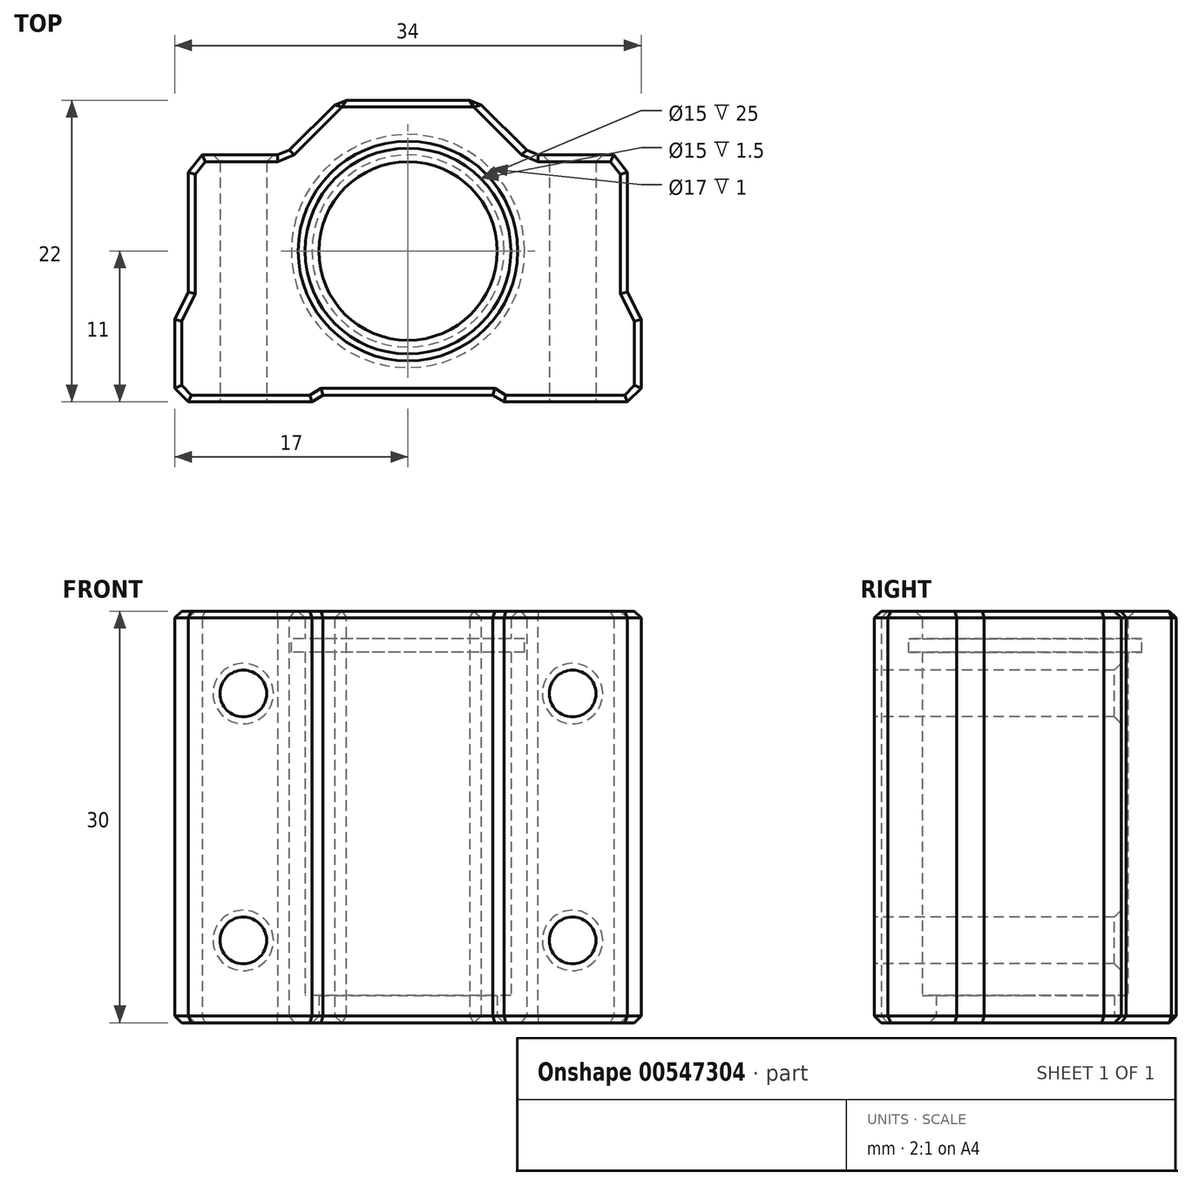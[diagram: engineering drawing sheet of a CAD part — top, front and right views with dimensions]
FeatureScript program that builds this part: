
annotation { "Feature Type Name" : "Feature", "Feature Type Description" : "" }
export const myFeature = defineFeature(function(context is Context, id is Id, definition is map)
    precondition{}
    {
        {
            var Q0;
            Q0=qCreatedBy(makeId("Top.planeOp"),FACE);
            var sketch = newSketch(context, id + "F0", { "sketchPlane" : qUnion([Q0])});
            skLineSegment(sketch, "E0", {"start": v(16, -11) * mm, "end": v(17, -10) * mm});
            skLineSegment(sketch, "E1", {"start": v(17, -10) * mm, "end": v(17, -5) * mm});
            skLineSegment(sketch, "E2", {"start": v(17, -5) * mm, "end": v(16, -3) * mm});
            skLineSegment(sketch, "E3", {"start": v(16, -3) * mm, "end": v(16, 5.75) * mm});
            skLineSegment(sketch, "E4", {"start": v(16, 5.75) * mm, "end": v(15, 7) * mm});
            skLineSegment(sketch, "E5", {"start": v(15, 7) * mm, "end": v(9, 7) * mm});
            skLineSegment(sketch, "E6", {"start": v(9, 7) * mm, "end": v(5, 11) * mm});
            skLineSegment(sketch, "E7", {"start": v(5, 11) * mm, "end": v(-5, 11) * mm});
            skLineSegment(sketch, "E8", {"start": v(-5, 11) * mm, "end": v(-9, 7) * mm});
            skLineSegment(sketch, "E9", {"start": v(-9, 7) * mm, "end": v(-15, 7) * mm});
            skLineSegment(sketch, "E10", {"start": v(-15, 7) * mm, "end": v(-16, 5.75) * mm});
            skLineSegment(sketch, "E11", {"start": v(-16, 5.75) * mm, "end": v(-16, -3) * mm});
            skLineSegment(sketch, "E12", {"start": v(-16, -3) * mm, "end": v(-17, -5) * mm});
            skLineSegment(sketch, "E13", {"start": v(-17, -5) * mm, "end": v(-17, -10) * mm});
            skLineSegment(sketch, "E14", {"start": v(-17, -10) * mm, "end": v(-16, -11) * mm});
            skCircle(sketch, "E15", {"center": v(0, 0) * mm, "radius": 7.5 * mm});
            skLineSegment(sketch, "E16", {"start": v(-16, -11) * mm, "end": v(-7, -11) * mm});
            skLineSegment(sketch, "E17", {"start": v(-7, -11) * mm, "end": v(-6.2, -10.5) * mm});
            skLineSegment(sketch, "E18", {"start": v(-6.2, -10.5) * mm, "end": v(6.2, -10.5) * mm});
            skLineSegment(sketch, "E19", {"start": v(6.2, -10.5) * mm, "end": v(7, -11) * mm});
            skLineSegment(sketch, "E20", {"start": v(7, -11) * mm, "end": v(16, -11) * mm});
            skSolve(sketch);
        }
        {
            var Q0;
            Q0 = qSketchRegion(id + "F0", true);
            extrude(context, id + "F1", {"entities" : qUnion([Q0]), "depth" : 15 * mm, "offsetDistance" : 25 * mm, "hasSecondDirection" : true, "secondDirectionOppositeDirection" : true, "secondDirectionDepth" : 15 * mm});
        }
        {
            var Q0;
            Q0=makeQuery(id+"F1.opExtrude","SWEPT_FACE",FACE,{"disambiguationData":[OSD([sQuery(id+"F0.wireOp",EDGE,"E16")])]});
            var sketch = newSketch(context, id + "F2", { "sketchPlane" : qUnion([Q0])});
            skCircle(sketch, "E21", {"center": v(-12, 9) * mm, "radius": 1.7 * mm});
            skCircle(sketch, "E22", {"center": v(-12, -9) * mm, "radius": 1.7 * mm});
            skCircle(sketch, "E23", {"center": v(12, 9) * mm, "radius": 1.7 * mm});
            skCircle(sketch, "E24", {"center": v(12, -9) * mm, "radius": 1.7 * mm});
            skSolve(sketch);
        }
        {
            var Q0;
            Q0=makeQuery(id+"F2.imprint","IMPRINT",FACE,{"disambiguationData":[TD([[makeQuery(id+"F2.imprint","IMPRINT",EDGE,{"derivedFrom":sQuery(id+"F2.wireOp",EDGE,"E21")}),1.0]])]});
            var Q1;
            Q1=makeQuery(id+"F2.imprint","IMPRINT",FACE,{"disambiguationData":[TD([[makeQuery(id+"F2.imprint","IMPRINT",EDGE,{"derivedFrom":sQuery(id+"F2.wireOp",EDGE,"E23")}),1.0]])]});
            var Q2;
            Q2=makeQuery(id+"F2.imprint","IMPRINT",FACE,{"disambiguationData":[TD([[makeQuery(id+"F2.imprint","IMPRINT",EDGE,{"derivedFrom":sQuery(id+"F2.wireOp",EDGE,"E24")}),1.0]])]});
            var Q3;
            Q3=makeQuery(id+"F2.imprint","IMPRINT",FACE,{"disambiguationData":[TD([[makeQuery(id+"F2.imprint","IMPRINT",EDGE,{"derivedFrom":sQuery(id+"F2.wireOp",EDGE,"E22")}),1.0]])]});
            var Q4;
            Q4=sQuery(id+"F2.wireOp",EDGE,"E22");
            var Q5;
            Q5=sQuery(id+"F2.wireOp",EDGE,"E21");
            var Q6;
            Q6=sQuery(id+"F2.wireOp",EDGE,"E23");
            var Q7;
            Q7=sQuery(id+"F2.wireOp",EDGE,"E24");
            extrude(context, id + "F3", {"entities" : qUnion([Q0, Q1, Q2, Q3]), "operationType" : NewBodyOperationType.REMOVE, "surfaceEntities" : qUnion([Q4, Q5, Q6, Q7]), "oppositeDirection" : true, "depth" : 25 * mm, "offsetDistance" : 25 * mm});
        }
        {
            var Q0;
            Q0=makeQuery(id+"F3.boolean.opBoolean","INTERSECT",EDGE,{"derivedFrom":[makeQuery(id+"F1.opExtrude","SWEPT_FACE",FACE,{"disambiguationData":[OSD([sQuery(id+"F0.wireOp",EDGE,"E9")])]}),makeQuery(id+"F3.opExtrude","SWEPT_FACE",FACE,{"disambiguationData":[OSD([sQuery(id+"F2.wireOp",EDGE,"E21")])]})]});
            var Q1;
            Q1=makeQuery(id+"F3.boolean.opBoolean","INTERSECT",EDGE,{"derivedFrom":[makeQuery(id+"F1.opExtrude","SWEPT_FACE",FACE,{"disambiguationData":[OSD([sQuery(id+"F0.wireOp",EDGE,"E9")])]}),makeQuery(id+"F3.opExtrude","SWEPT_FACE",FACE,{"disambiguationData":[OSD([sQuery(id+"F2.wireOp",EDGE,"E22")])]})]});
            var Q2;
            Q2=makeQuery(id+"F3.boolean.opBoolean","INTERSECT",EDGE,{"derivedFrom":[makeQuery(id+"F1.opExtrude","SWEPT_FACE",FACE,{"disambiguationData":[OSD([sQuery(id+"F0.wireOp",EDGE,"E5")])]}),makeQuery(id+"F3.opExtrude","SWEPT_FACE",FACE,{"disambiguationData":[OSD([sQuery(id+"F2.wireOp",EDGE,"E24")])]})]});
            var Q3;
            Q3=makeQuery(id+"F3.boolean.opBoolean","INTERSECT",EDGE,{"derivedFrom":[makeQuery(id+"F1.opExtrude","SWEPT_FACE",FACE,{"disambiguationData":[OSD([sQuery(id+"F0.wireOp",EDGE,"E5")])]}),makeQuery(id+"F3.opExtrude","SWEPT_FACE",FACE,{"disambiguationData":[OSD([sQuery(id+"F2.wireOp",EDGE,"E23")])]})]});
            var Q4;
            Q4=makeQuery(id+"F3.boolean.opBoolean","COPY",EDGE,{"derivedFrom":makeQuery(id+"F3.opExtrude","CAP_EDGE",EDGE,{"disambiguationData":[OSD([sQuery(id+"F2.wireOp",EDGE,"E21")])],"isStart":true})});
            var Q5;
            Q5=makeQuery(id+"F3.boolean.opBoolean","COPY",EDGE,{"derivedFrom":makeQuery(id+"F3.opExtrude","CAP_EDGE",EDGE,{"disambiguationData":[OSD([sQuery(id+"F2.wireOp",EDGE,"E22")])],"isStart":true})});
            var Q6;
            Q6=makeQuery(id+"F3.boolean.opBoolean","COPY",EDGE,{"derivedFrom":makeQuery(id+"F3.opExtrude","CAP_EDGE",EDGE,{"disambiguationData":[OSD([sQuery(id+"F2.wireOp",EDGE,"E24")])],"isStart":true})});
            var Q7;
            Q7=makeQuery(id+"F3.boolean.opBoolean","COPY",EDGE,{"derivedFrom":makeQuery(id+"F3.opExtrude","CAP_EDGE",EDGE,{"disambiguationData":[OSD([sQuery(id+"F2.wireOp",EDGE,"E23")])],"isStart":true})});
            chamfer(context, id + "F4", {"entities" : qUnion([Q0, Q1, Q2, Q3, Q4, Q5, Q6, Q7]), "width" : .5 * mm, "tangentPropagation" : true});
        }
        {
            var Q0;
            Q0=makeQuery(id+"F1.opExtrude","CAP_FACE",FACE,{"disambiguationData":[OSD([sQuery(id+"F0.wireOp",EDGE,"E0"),sQuery(id+"F0.wireOp",EDGE,"E1"),sQuery(id+"F0.wireOp",EDGE,"E2"),sQuery(id+"F0.wireOp",EDGE,"E3"),sQuery(id+"F0.wireOp",EDGE,"E4"),sQuery(id+"F0.wireOp",EDGE,"E5"),sQuery(id+"F0.wireOp",EDGE,"E6"),sQuery(id+"F0.wireOp",EDGE,"E7"),sQuery(id+"F0.wireOp",EDGE,"E8"),sQuery(id+"F0.wireOp",EDGE,"E9"),sQuery(id+"F0.wireOp",EDGE,"E10"),sQuery(id+"F0.wireOp",EDGE,"E11"),sQuery(id+"F0.wireOp",EDGE,"E12"),sQuery(id+"F0.wireOp",EDGE,"E13"),sQuery(id+"F0.wireOp",EDGE,"E14"),sQuery(id+"F0.wireOp",EDGE,"E15"),sQuery(id+"F0.wireOp",EDGE,"E16"),sQuery(id+"F0.wireOp",EDGE,"E17"),sQuery(id+"F0.wireOp",EDGE,"E18"),sQuery(id+"F0.wireOp",EDGE,"E19"),sQuery(id+"F0.wireOp",EDGE,"E20")])],"isStart":true});
            var sketch = newSketch(context, id + "F5", { "sketchPlane" : qUnion([Q0])});
            skCircle(sketch, "E25", {"center": v(0, 0) * mm, "radius": 6.5 * mm});
            skSolve(sketch);
        }
        {
            var Q0;
            Q0=makeQuery(id+"F5.imprint","IMPRINT",FACE,{"disambiguationData":[TD([[makeQuery(id+"F5.imprint","IMPRINT",EDGE,{"derivedFrom":sQuery(id+"F5.wireOp",EDGE,"E25")}),-1.0]])]});
            extrude(context, id + "F6", {"entities" : qUnion([Q0]), "operationType" : NewBodyOperationType.ADD, "oppositeDirection" : true, "depth" : 2 * mm, "offsetDistance" : 25 * mm});
        }
        {
            var Q0;
            Q0=makeQuery(id+"F1.opExtrude","CAP_FACE",FACE,{"disambiguationData":[OSD([sQuery(id+"F0.wireOp",EDGE,"E0"),sQuery(id+"F0.wireOp",EDGE,"E1"),sQuery(id+"F0.wireOp",EDGE,"E2"),sQuery(id+"F0.wireOp",EDGE,"E3"),sQuery(id+"F0.wireOp",EDGE,"E4"),sQuery(id+"F0.wireOp",EDGE,"E5"),sQuery(id+"F0.wireOp",EDGE,"E6"),sQuery(id+"F0.wireOp",EDGE,"E7"),sQuery(id+"F0.wireOp",EDGE,"E8"),sQuery(id+"F0.wireOp",EDGE,"E9"),sQuery(id+"F0.wireOp",EDGE,"E10"),sQuery(id+"F0.wireOp",EDGE,"E11"),sQuery(id+"F0.wireOp",EDGE,"E12"),sQuery(id+"F0.wireOp",EDGE,"E13"),sQuery(id+"F0.wireOp",EDGE,"E14"),sQuery(id+"F0.wireOp",EDGE,"E15"),sQuery(id+"F0.wireOp",EDGE,"E16"),sQuery(id+"F0.wireOp",EDGE,"E17"),sQuery(id+"F0.wireOp",EDGE,"E18"),sQuery(id+"F0.wireOp",EDGE,"E19"),sQuery(id+"F0.wireOp",EDGE,"E20")])],"isStart":false});
            cPlane(context, id + "F7", {"entities" : qUnion([Q0]), "cplaneType" : CPlaneType.OFFSET, "offset" : 2 * mm, "oppositeDirection" : true, "width" : 150 * mm, "height" : 150 * mm});
        }
        {
            var Q0;
            Q0=qCreatedBy(id+"F7.planeOp",FACE);
            var sketch = newSketch(context, id + "F8", { "sketchPlane" : qUnion([Q0])});
            skCircle(sketch, "E26", {"center": v(0, 0) * mm, "radius": 8.5 * mm});
            skSolve(sketch);
        }
        {
            var Q0;
            Q0 = qSketchRegion(id + "F8", true);
            extrude(context, id + "F9", {"entities" : qUnion([Q0]), "operationType" : NewBodyOperationType.REMOVE, "oppositeDirection" : true, "depth" : 1 * mm, "offsetDistance" : 25 * mm});
        }
        {
            var Q0;
            Q0=makeQuery(id+"F1.opExtrude","CAP_FACE",FACE,{"disambiguationData":[OSD([sQuery(id+"F0.wireOp",EDGE,"E0"),sQuery(id+"F0.wireOp",EDGE,"E1"),sQuery(id+"F0.wireOp",EDGE,"E2"),sQuery(id+"F0.wireOp",EDGE,"E3"),sQuery(id+"F0.wireOp",EDGE,"E4"),sQuery(id+"F0.wireOp",EDGE,"E5"),sQuery(id+"F0.wireOp",EDGE,"E6"),sQuery(id+"F0.wireOp",EDGE,"E7"),sQuery(id+"F0.wireOp",EDGE,"E8"),sQuery(id+"F0.wireOp",EDGE,"E9"),sQuery(id+"F0.wireOp",EDGE,"E10"),sQuery(id+"F0.wireOp",EDGE,"E11"),sQuery(id+"F0.wireOp",EDGE,"E12"),sQuery(id+"F0.wireOp",EDGE,"E13"),sQuery(id+"F0.wireOp",EDGE,"E14"),sQuery(id+"F0.wireOp",EDGE,"E15"),sQuery(id+"F0.wireOp",EDGE,"E16"),sQuery(id+"F0.wireOp",EDGE,"E17"),sQuery(id+"F0.wireOp",EDGE,"E18"),sQuery(id+"F0.wireOp",EDGE,"E19"),sQuery(id+"F0.wireOp",EDGE,"E20")])],"isStart":false});
            var Q1;
            {var subQ0=sQuery(id+"F0.wireOp",EDGE,"E15");Q1=makeQuery(id+"F6.boolean.opBoolean","MERGE",FACE,{"derivedFrom":[makeQuery(id+"F1.opExtrude","CAP_FACE",FACE,{"disambiguationData":[OSD([sQuery(id+"F0.wireOp",EDGE,"E0"),sQuery(id+"F0.wireOp",EDGE,"E1"),sQuery(id+"F0.wireOp",EDGE,"E2"),sQuery(id+"F0.wireOp",EDGE,"E3"),sQuery(id+"F0.wireOp",EDGE,"E4"),sQuery(id+"F0.wireOp",EDGE,"E5"),sQuery(id+"F0.wireOp",EDGE,"E6"),sQuery(id+"F0.wireOp",EDGE,"E7"),sQuery(id+"F0.wireOp",EDGE,"E8"),sQuery(id+"F0.wireOp",EDGE,"E9"),sQuery(id+"F0.wireOp",EDGE,"E10"),sQuery(id+"F0.wireOp",EDGE,"E11"),sQuery(id+"F0.wireOp",EDGE,"E12"),sQuery(id+"F0.wireOp",EDGE,"E13"),sQuery(id+"F0.wireOp",EDGE,"E14"),subQ0,sQuery(id+"F0.wireOp",EDGE,"E16"),sQuery(id+"F0.wireOp",EDGE,"E17"),sQuery(id+"F0.wireOp",EDGE,"E18"),sQuery(id+"F0.wireOp",EDGE,"E19"),sQuery(id+"F0.wireOp",EDGE,"E20")])],"isStart":true}),makeQuery(id+"F6.opExtrude","CAP_FACE",FACE,{"disambiguationData":[OSD([subQ0,sQuery(id+"F5.wireOp",EDGE,"E25")])],"isStart":true})]});}
            var Q2;
            Q2=makeQuery(id+"F1.opExtrude","SWEPT_EDGE",EDGE,{"disambiguationData":[OSD([sQuery(id+"F0.wireOp",EDGE,"E8"),sQuery(id+"F0.wireOp",EDGE,"E9")])]});
            var Q3;
            Q3=makeQuery(id+"F1.opExtrude","SWEPT_EDGE",EDGE,{"disambiguationData":[OSD([sQuery(id+"F0.wireOp",EDGE,"E7"),sQuery(id+"F0.wireOp",EDGE,"E8")])]});
            var Q4;
            Q4=makeQuery(id+"F1.opExtrude","SWEPT_EDGE",EDGE,{"disambiguationData":[OSD([sQuery(id+"F0.wireOp",EDGE,"E6"),sQuery(id+"F0.wireOp",EDGE,"E7")])]});
            var Q5;
            Q5=makeQuery(id+"F1.opExtrude","SWEPT_EDGE",EDGE,{"disambiguationData":[OSD([sQuery(id+"F0.wireOp",EDGE,"E5"),sQuery(id+"F0.wireOp",EDGE,"E6")])]});
            chamfer(context, id + "F10", {"entities" : qUnion([Q0, Q1, Q2, Q3, Q4, Q5]), "width" : .5 * mm, "tangentPropagation" : true});
        }
    });
